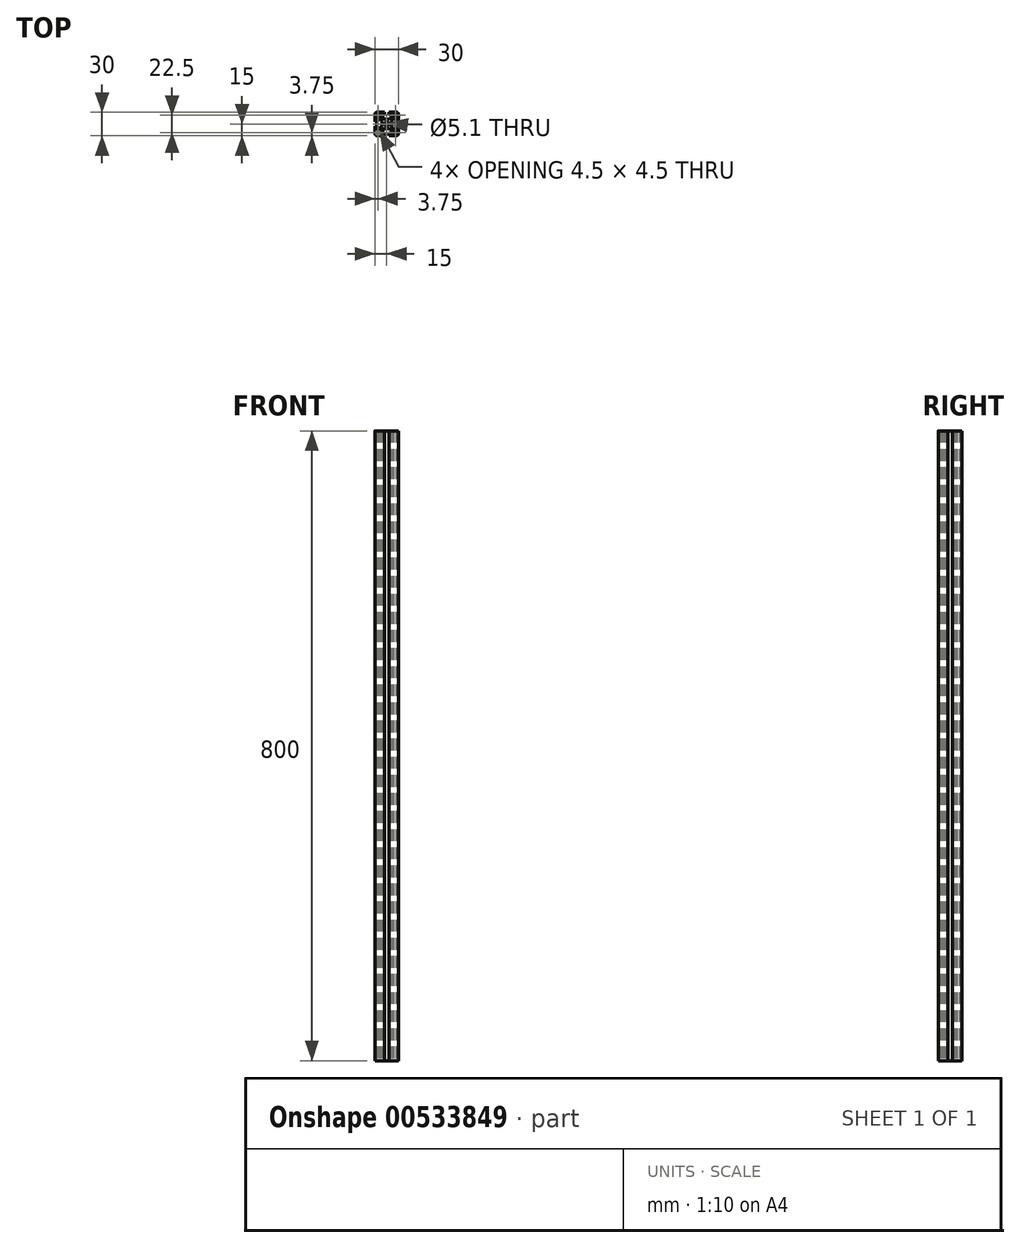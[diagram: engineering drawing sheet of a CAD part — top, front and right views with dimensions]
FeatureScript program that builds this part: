
annotation { "Feature Type Name" : "Feature", "Feature Type Description" : "" }
export const myFeature = defineFeature(function(context is Context, id is Id, definition is map)
    precondition{}
    {
        {
            var Q0;
            Q0=qCreatedBy(makeId("Top.planeOp"),FACE);
            var sketch = newSketch(context, id + "F0", { "sketchPlane" : qUnion([Q0])});
            skLineSegment(sketch, "E0", {"start": v(20, 4) * mm, "end": v(15.5, 4) * mm});
            skLineSegment(sketch, "E1", {"start": v(20, 16) * mm, "end": v(20, 4) * mm});
            skArc(sketch, "E2", {"start": v(16, 20) * mm, "mid": v(18.83, 18.83) * mm, "end": v(20, 16) * mm});
            skLineSegment(sketch, "E3", {"start": v(4, 20) * mm, "end": v(16, 20) * mm});
            skLineSegment(sketch, "E4", {"start": v(4, 20) * mm, "end": v(4, 15.5) * mm});
            skLineSegment(sketch, "E5", {"start": v(4, 15.5) * mm, "end": v(6.72, 15.5) * mm});
            skLineSegment(sketch, "E6", {"start": v(6.72, 17.35) * mm, "end": v(6.72, 15.5) * mm});
            skLineSegment(sketch, "E7", {"start": v(10.22, 17.35) * mm, "end": v(6.72, 17.35) * mm});
            skLineSegment(sketch, "E8", {"start": v(10.22, 12) * mm, "end": v(10.22, 17.35) * mm});
            skLineSegment(sketch, "E9", {"start": v(4, 7.75) * mm, "end": v(10.22, 12) * mm});
            skLineSegment(sketch, "E10", {"start": v(-4, 7.75) * mm, "end": v(4, 7.75) * mm});
            skLineSegment(sketch, "E11", {"start": v(-4, 7.75) * mm, "end": v(-10.22, 12) * mm});
            skLineSegment(sketch, "E12", {"start": v(-10.22, 12) * mm, "end": v(-10.22, 17.35) * mm});
            skLineSegment(sketch, "E13", {"start": v(-10.22, 17.35) * mm, "end": v(-6.72, 17.35) * mm});
            skLineSegment(sketch, "E14", {"start": v(-6.72, 15.5) * mm, "end": v(-6.72, 17.35) * mm});
            skLineSegment(sketch, "E15", {"start": v(-4, 15.5) * mm, "end": v(-6.72, 15.5) * mm});
            skLineSegment(sketch, "E16", {"start": v(-4, 20) * mm, "end": v(-4, 15.5) * mm});
            skLineSegment(sketch, "E17", {"start": v(-16, 20) * mm, "end": v(-4, 20) * mm});
            skArc(sketch, "E18", {"start": v(-16, 20) * mm, "mid": v(-18.83, 18.83) * mm, "end": v(-20, 16) * mm});
            skLineSegment(sketch, "E19", {"start": v(-20, 16) * mm, "end": v(-20, 4) * mm});
            skLineSegment(sketch, "E20", {"start": v(-20, 4) * mm, "end": v(-15.5, 4) * mm});
            skLineSegment(sketch, "E21", {"start": v(-15.5, 4) * mm, "end": v(-15.5, 6.72) * mm});
            skLineSegment(sketch, "E22", {"start": v(-17.35, 6.72) * mm, "end": v(-15.5, 6.72) * mm});
            skLineSegment(sketch, "E23", {"start": v(-17.35, 10.22) * mm, "end": v(-17.35, 6.72) * mm});
            skLineSegment(sketch, "E24", {"start": v(-12, 10.22) * mm, "end": v(-17.35, 10.22) * mm});
            skLineSegment(sketch, "E25", {"start": v(-7.75, 4) * mm, "end": v(-12, 10.22) * mm});
            skLineSegment(sketch, "E26", {"start": v(-7.75, -4) * mm, "end": v(-7.75, 4) * mm});
            skLineSegment(sketch, "E27", {"start": v(-7.75, -4) * mm, "end": v(-12, -10.22) * mm});
            skLineSegment(sketch, "E28", {"start": v(-12, -10.22) * mm, "end": v(-17.35, -10.22) * mm});
            skLineSegment(sketch, "E29", {"start": v(-17.35, -10.22) * mm, "end": v(-17.35, -6.72) * mm});
            skLineSegment(sketch, "E30", {"start": v(-17.35, -6.72) * mm, "end": v(-15.5, -6.72) * mm});
            skLineSegment(sketch, "E31", {"start": v(-15.5, -4) * mm, "end": v(-15.5, -6.72) * mm});
            skLineSegment(sketch, "E32", {"start": v(-20, -4) * mm, "end": v(-15.5, -4) * mm});
            skLineSegment(sketch, "E33", {"start": v(-20, -4) * mm, "end": v(-20, -16) * mm});
            skArc(sketch, "E34", {"start": v(-20, -16) * mm, "mid": v(-18.83, -18.83) * mm, "end": v(-16, -20) * mm});
            skLineSegment(sketch, "E35", {"start": v(-16, -20) * mm, "end": v(-4, -20) * mm});
            skLineSegment(sketch, "E36", {"start": v(-4, -20) * mm, "end": v(-4, -15.5) * mm});
            skLineSegment(sketch, "E37", {"start": v(-4, -15.5) * mm, "end": v(-6.72, -15.5) * mm});
            skLineSegment(sketch, "E38", {"start": v(-6.72, -17.35) * mm, "end": v(-6.72, -15.5) * mm});
            skLineSegment(sketch, "E39", {"start": v(-10.22, -17.35) * mm, "end": v(-6.72, -17.35) * mm});
            skLineSegment(sketch, "E40", {"start": v(-10.22, -12) * mm, "end": v(-10.22, -17.35) * mm});
            skLineSegment(sketch, "E41", {"start": v(-4, -7.75) * mm, "end": v(-10.22, -12) * mm});
            skLineSegment(sketch, "E42", {"start": v(4, -7.75) * mm, "end": v(-4, -7.75) * mm});
            skLineSegment(sketch, "E43", {"start": v(4, -7.75) * mm, "end": v(10.22, -12) * mm});
            skLineSegment(sketch, "E44", {"start": v(10.22, -12) * mm, "end": v(10.22, -17.35) * mm});
            skLineSegment(sketch, "E45", {"start": v(10.22, -17.35) * mm, "end": v(6.72, -17.35) * mm});
            skLineSegment(sketch, "E46", {"start": v(6.72, -15.5) * mm, "end": v(6.72, -17.35) * mm});
            skLineSegment(sketch, "E47", {"start": v(4, -15.5) * mm, "end": v(6.72, -15.5) * mm});
            skLineSegment(sketch, "E48", {"start": v(4, -20) * mm, "end": v(4, -15.5) * mm});
            skLineSegment(sketch, "E49", {"start": v(4, -20) * mm, "end": v(16, -20) * mm});
            skArc(sketch, "E50", {"start": v(16, -20) * mm, "mid": v(18.83, -18.83) * mm, "end": v(20, -16) * mm});
            skLineSegment(sketch, "E51", {"start": v(20, -4) * mm, "end": v(20, -16) * mm});
            skLineSegment(sketch, "E52", {"start": v(20, -4) * mm, "end": v(15.5, -4) * mm});
            skLineSegment(sketch, "E53", {"start": v(15.5, -4) * mm, "end": v(15.5, -6.72) * mm});
            skLineSegment(sketch, "E54", {"start": v(17.35, -6.72) * mm, "end": v(15.5, -6.72) * mm});
            skLineSegment(sketch, "E55", {"start": v(17.35, -10.22) * mm, "end": v(17.35, -6.72) * mm});
            skLineSegment(sketch, "E56", {"start": v(12, -10.22) * mm, "end": v(17.35, -10.22) * mm});
            skLineSegment(sketch, "E57", {"start": v(7.75, -4) * mm, "end": v(12, -10.22) * mm});
            skLineSegment(sketch, "E58", {"start": v(7.75, 4) * mm, "end": v(7.75, -4) * mm});
            skLineSegment(sketch, "E59", {"start": v(7.75, 4) * mm, "end": v(12, 10.22) * mm});
            skLineSegment(sketch, "E60", {"start": v(12, 10.22) * mm, "end": v(17.35, 10.22) * mm});
            skLineSegment(sketch, "E61", {"start": v(17.35, 10.22) * mm, "end": v(17.35, 6.72) * mm});
            skLineSegment(sketch, "E62", {"start": v(15.5, 6.72) * mm, "end": v(17.35, 6.72) * mm});
            skLineSegment(sketch, "E63", {"start": v(15.5, 4) * mm, "end": v(15.5, 6.72) * mm});
            skLineSegment(sketch, "E64", {"start": v(18, 12) * mm, "end": v(18, 16) * mm});
            skLineSegment(sketch, "E65", {"start": v(12, 12) * mm, "end": v(18, 12) * mm});
            skLineSegment(sketch, "E66", {"start": v(12, 18) * mm, "end": v(12, 12) * mm});
            skLineSegment(sketch, "E67", {"start": v(16, 18) * mm, "end": v(12, 18) * mm});
            skArc(sketch, "E68", {"start": v(18, 16) * mm, "mid": v(17.41, 17.41) * mm, "end": v(16, 18) * mm});
            skLineSegment(sketch, "E69", {"start": v(-18, -12) * mm, "end": v(-18, -16) * mm});
            skLineSegment(sketch, "E70", {"start": v(-12, -12) * mm, "end": v(-18, -12) * mm});
            skLineSegment(sketch, "E71", {"start": v(-12, -18) * mm, "end": v(-12, -12) * mm});
            skLineSegment(sketch, "E72", {"start": v(-16, -18) * mm, "end": v(-12, -18) * mm});
            skArc(sketch, "E73", {"start": v(-18, -16) * mm, "mid": v(-17.41, -17.41) * mm, "end": v(-16, -18) * mm});
            skLineSegment(sketch, "E74", {"start": v(12, -18) * mm, "end": v(16, -18) * mm});
            skLineSegment(sketch, "E75", {"start": v(12, -12) * mm, "end": v(12, -18) * mm});
            skLineSegment(sketch, "E76", {"start": v(18, -12) * mm, "end": v(12, -12) * mm});
            skLineSegment(sketch, "E77", {"start": v(18, -16) * mm, "end": v(18, -12) * mm});
            skArc(sketch, "E78", {"start": v(16, -18) * mm, "mid": v(17.41, -17.41) * mm, "end": v(18, -16) * mm});
            skLineSegment(sketch, "E79", {"start": v(-12, 18) * mm, "end": v(-16, 18) * mm});
            skLineSegment(sketch, "E80", {"start": v(-12, 12) * mm, "end": v(-12, 18) * mm});
            skLineSegment(sketch, "E81", {"start": v(-18, 12) * mm, "end": v(-12, 12) * mm});
            skLineSegment(sketch, "E82", {"start": v(-18, 16) * mm, "end": v(-18, 12) * mm});
            skArc(sketch, "E83", {"start": v(-16, 18) * mm, "mid": v(-17.41, 17.41) * mm, "end": v(-18, 16) * mm});
            skCircle(sketch, "E84", {"center": v(0, 0) * mm, "radius": 3.4 * mm});
            skSolve(sketch);
        }
        {
            var Q0;
            Q0=makeQuery(id+"F0.imprint","IMPRINT",FACE,{"disambiguationData":[TD([[makeQuery(id+"F0.imprint","IMPRINT",EDGE,{"derivedFrom":sQuery(id+"F0.wireOp",EDGE,"E0")}),-1.0]])]});
            extrude(context, id + "F1", {"entities" : qUnion([Q0]), "depth" : 400 * mm, "offsetDistance" : 25 * mm});
        }
        {
            var Q0;
            Q0=makeQuery(id+"F1.opExtrude","SWEPT_BODY",BODY,{"disambiguationData":[OSD([sQuery(id+"F0.wireOp",EDGE,"E0"),sQuery(id+"F0.wireOp",EDGE,"E1"),sQuery(id+"F0.wireOp",EDGE,"E2"),sQuery(id+"F0.wireOp",EDGE,"E3"),sQuery(id+"F0.wireOp",EDGE,"E4"),sQuery(id+"F0.wireOp",EDGE,"E5"),sQuery(id+"F0.wireOp",EDGE,"E6"),sQuery(id+"F0.wireOp",EDGE,"E7"),sQuery(id+"F0.wireOp",EDGE,"E8"),sQuery(id+"F0.wireOp",EDGE,"E9"),sQuery(id+"F0.wireOp",EDGE,"E10"),sQuery(id+"F0.wireOp",EDGE,"E11"),sQuery(id+"F0.wireOp",EDGE,"E12"),sQuery(id+"F0.wireOp",EDGE,"E13"),sQuery(id+"F0.wireOp",EDGE,"E14"),sQuery(id+"F0.wireOp",EDGE,"E15"),sQuery(id+"F0.wireOp",EDGE,"E16"),sQuery(id+"F0.wireOp",EDGE,"E17"),sQuery(id+"F0.wireOp",EDGE,"E18"),sQuery(id+"F0.wireOp",EDGE,"E19"),sQuery(id+"F0.wireOp",EDGE,"E20"),sQuery(id+"F0.wireOp",EDGE,"E21"),sQuery(id+"F0.wireOp",EDGE,"E22"),sQuery(id+"F0.wireOp",EDGE,"E23"),sQuery(id+"F0.wireOp",EDGE,"E24"),sQuery(id+"F0.wireOp",EDGE,"E25"),sQuery(id+"F0.wireOp",EDGE,"E26"),sQuery(id+"F0.wireOp",EDGE,"E27"),sQuery(id+"F0.wireOp",EDGE,"E28"),sQuery(id+"F0.wireOp",EDGE,"E29"),sQuery(id+"F0.wireOp",EDGE,"E30"),sQuery(id+"F0.wireOp",EDGE,"E31"),sQuery(id+"F0.wireOp",EDGE,"E32"),sQuery(id+"F0.wireOp",EDGE,"E33"),sQuery(id+"F0.wireOp",EDGE,"E34"),sQuery(id+"F0.wireOp",EDGE,"E35"),sQuery(id+"F0.wireOp",EDGE,"E36"),sQuery(id+"F0.wireOp",EDGE,"E37"),sQuery(id+"F0.wireOp",EDGE,"E38"),sQuery(id+"F0.wireOp",EDGE,"E39"),sQuery(id+"F0.wireOp",EDGE,"E40"),sQuery(id+"F0.wireOp",EDGE,"E41"),sQuery(id+"F0.wireOp",EDGE,"E42"),sQuery(id+"F0.wireOp",EDGE,"E43"),sQuery(id+"F0.wireOp",EDGE,"E44"),sQuery(id+"F0.wireOp",EDGE,"E45"),sQuery(id+"F0.wireOp",EDGE,"E46"),sQuery(id+"F0.wireOp",EDGE,"E47"),sQuery(id+"F0.wireOp",EDGE,"E48"),sQuery(id+"F0.wireOp",EDGE,"E49"),sQuery(id+"F0.wireOp",EDGE,"E50"),sQuery(id+"F0.wireOp",EDGE,"E51"),sQuery(id+"F0.wireOp",EDGE,"E52"),sQuery(id+"F0.wireOp",EDGE,"E53"),sQuery(id+"F0.wireOp",EDGE,"E54"),sQuery(id+"F0.wireOp",EDGE,"E55"),sQuery(id+"F0.wireOp",EDGE,"E56"),sQuery(id+"F0.wireOp",EDGE,"E57"),sQuery(id+"F0.wireOp",EDGE,"E58"),sQuery(id+"F0.wireOp",EDGE,"E59"),sQuery(id+"F0.wireOp",EDGE,"E60"),sQuery(id+"F0.wireOp",EDGE,"E61"),sQuery(id+"F0.wireOp",EDGE,"E62"),sQuery(id+"F0.wireOp",EDGE,"E63"),sQuery(id+"F0.wireOp",EDGE,"E64"),sQuery(id+"F0.wireOp",EDGE,"E65"),sQuery(id+"F0.wireOp",EDGE,"E66"),sQuery(id+"F0.wireOp",EDGE,"E67"),sQuery(id+"F0.wireOp",EDGE,"E68"),sQuery(id+"F0.wireOp",EDGE,"E69"),sQuery(id+"F0.wireOp",EDGE,"E70"),sQuery(id+"F0.wireOp",EDGE,"E71"),sQuery(id+"F0.wireOp",EDGE,"E72"),sQuery(id+"F0.wireOp",EDGE,"E73"),sQuery(id+"F0.wireOp",EDGE,"E74"),sQuery(id+"F0.wireOp",EDGE,"E75"),sQuery(id+"F0.wireOp",EDGE,"E76"),sQuery(id+"F0.wireOp",EDGE,"E77"),sQuery(id+"F0.wireOp",EDGE,"E78"),sQuery(id+"F0.wireOp",EDGE,"E79"),sQuery(id+"F0.wireOp",EDGE,"E80"),sQuery(id+"F0.wireOp",EDGE,"E81"),sQuery(id+"F0.wireOp",EDGE,"E82"),sQuery(id+"F0.wireOp",EDGE,"E83"),sQuery(id+"F0.wireOp",EDGE,"E84")])]});
            var Q1;
            Q1=makeQuery(id+"F1.opExtrude","CAP_VERTEX",VERTEX,{"disambiguationData":[OSD([sQuery(id+"F0.wireOp",EDGE,"E51"),sQuery(id+"F0.wireOp",EDGE,"E52")])],"isStart":true});
            transform(context, id + "F2", {"entities" : qUnion([Q0]), "transformType" : TransformType.SCALE_UNIFORMLY, "scale" : 3 / 4, "scalePoint" : qUnion([Q1]), "makeCopy" : false});
        }
        {
            var Q0;
            Q0=makeQuery(id+"F1.opExtrude","CAP_FACE",FACE,{"disambiguationData":[OSD([sQuery(id+"F0.wireOp",EDGE,"E0"),sQuery(id+"F0.wireOp",EDGE,"E1"),sQuery(id+"F0.wireOp",EDGE,"E2"),sQuery(id+"F0.wireOp",EDGE,"E3"),sQuery(id+"F0.wireOp",EDGE,"E4"),sQuery(id+"F0.wireOp",EDGE,"E5"),sQuery(id+"F0.wireOp",EDGE,"E6"),sQuery(id+"F0.wireOp",EDGE,"E7"),sQuery(id+"F0.wireOp",EDGE,"E8"),sQuery(id+"F0.wireOp",EDGE,"E9"),sQuery(id+"F0.wireOp",EDGE,"E10"),sQuery(id+"F0.wireOp",EDGE,"E11"),sQuery(id+"F0.wireOp",EDGE,"E12"),sQuery(id+"F0.wireOp",EDGE,"E13"),sQuery(id+"F0.wireOp",EDGE,"E14"),sQuery(id+"F0.wireOp",EDGE,"E15"),sQuery(id+"F0.wireOp",EDGE,"E16"),sQuery(id+"F0.wireOp",EDGE,"E17"),sQuery(id+"F0.wireOp",EDGE,"E18"),sQuery(id+"F0.wireOp",EDGE,"E19"),sQuery(id+"F0.wireOp",EDGE,"E20"),sQuery(id+"F0.wireOp",EDGE,"E21"),sQuery(id+"F0.wireOp",EDGE,"E22"),sQuery(id+"F0.wireOp",EDGE,"E23"),sQuery(id+"F0.wireOp",EDGE,"E24"),sQuery(id+"F0.wireOp",EDGE,"E25"),sQuery(id+"F0.wireOp",EDGE,"E26"),sQuery(id+"F0.wireOp",EDGE,"E27"),sQuery(id+"F0.wireOp",EDGE,"E28"),sQuery(id+"F0.wireOp",EDGE,"E29"),sQuery(id+"F0.wireOp",EDGE,"E30"),sQuery(id+"F0.wireOp",EDGE,"E31"),sQuery(id+"F0.wireOp",EDGE,"E32"),sQuery(id+"F0.wireOp",EDGE,"E33"),sQuery(id+"F0.wireOp",EDGE,"E34"),sQuery(id+"F0.wireOp",EDGE,"E35"),sQuery(id+"F0.wireOp",EDGE,"E36"),sQuery(id+"F0.wireOp",EDGE,"E37"),sQuery(id+"F0.wireOp",EDGE,"E38"),sQuery(id+"F0.wireOp",EDGE,"E39"),sQuery(id+"F0.wireOp",EDGE,"E40"),sQuery(id+"F0.wireOp",EDGE,"E41"),sQuery(id+"F0.wireOp",EDGE,"E42"),sQuery(id+"F0.wireOp",EDGE,"E43"),sQuery(id+"F0.wireOp",EDGE,"E44"),sQuery(id+"F0.wireOp",EDGE,"E45"),sQuery(id+"F0.wireOp",EDGE,"E46"),sQuery(id+"F0.wireOp",EDGE,"E47"),sQuery(id+"F0.wireOp",EDGE,"E48"),sQuery(id+"F0.wireOp",EDGE,"E49"),sQuery(id+"F0.wireOp",EDGE,"E50"),sQuery(id+"F0.wireOp",EDGE,"E51"),sQuery(id+"F0.wireOp",EDGE,"E52"),sQuery(id+"F0.wireOp",EDGE,"E53"),sQuery(id+"F0.wireOp",EDGE,"E54"),sQuery(id+"F0.wireOp",EDGE,"E55"),sQuery(id+"F0.wireOp",EDGE,"E56"),sQuery(id+"F0.wireOp",EDGE,"E57"),sQuery(id+"F0.wireOp",EDGE,"E58"),sQuery(id+"F0.wireOp",EDGE,"E59"),sQuery(id+"F0.wireOp",EDGE,"E60"),sQuery(id+"F0.wireOp",EDGE,"E61"),sQuery(id+"F0.wireOp",EDGE,"E62"),sQuery(id+"F0.wireOp",EDGE,"E63"),sQuery(id+"F0.wireOp",EDGE,"E64"),sQuery(id+"F0.wireOp",EDGE,"E65"),sQuery(id+"F0.wireOp",EDGE,"E66"),sQuery(id+"F0.wireOp",EDGE,"E67"),sQuery(id+"F0.wireOp",EDGE,"E68"),sQuery(id+"F0.wireOp",EDGE,"E69"),sQuery(id+"F0.wireOp",EDGE,"E70"),sQuery(id+"F0.wireOp",EDGE,"E71"),sQuery(id+"F0.wireOp",EDGE,"E72"),sQuery(id+"F0.wireOp",EDGE,"E73"),sQuery(id+"F0.wireOp",EDGE,"E74"),sQuery(id+"F0.wireOp",EDGE,"E75"),sQuery(id+"F0.wireOp",EDGE,"E76"),sQuery(id+"F0.wireOp",EDGE,"E77"),sQuery(id+"F0.wireOp",EDGE,"E78"),sQuery(id+"F0.wireOp",EDGE,"E79"),sQuery(id+"F0.wireOp",EDGE,"E80"),sQuery(id+"F0.wireOp",EDGE,"E81"),sQuery(id+"F0.wireOp",EDGE,"E82"),sQuery(id+"F0.wireOp",EDGE,"E83"),sQuery(id+"F0.wireOp",EDGE,"E84")])],"isStart":false});
            extrude(context, id + "F3", {"entities" : qUnion([Q0]), "operationType" : NewBodyOperationType.ADD, "depth" : 100 * mm, "offsetDistance" : 25 * mm});
        }
        {
            var Q0;
            Q0=makeQuery(id+"F3.opExtrude","CAP_FACE",FACE,{"disambiguationData":[OSD([sQuery(id+"F0.wireOp",EDGE,"E0"),sQuery(id+"F0.wireOp",EDGE,"E1"),sQuery(id+"F0.wireOp",EDGE,"E2"),sQuery(id+"F0.wireOp",EDGE,"E3"),sQuery(id+"F0.wireOp",EDGE,"E4"),sQuery(id+"F0.wireOp",EDGE,"E5"),sQuery(id+"F0.wireOp",EDGE,"E6"),sQuery(id+"F0.wireOp",EDGE,"E7"),sQuery(id+"F0.wireOp",EDGE,"E8"),sQuery(id+"F0.wireOp",EDGE,"E9"),sQuery(id+"F0.wireOp",EDGE,"E10"),sQuery(id+"F0.wireOp",EDGE,"E11"),sQuery(id+"F0.wireOp",EDGE,"E12"),sQuery(id+"F0.wireOp",EDGE,"E13"),sQuery(id+"F0.wireOp",EDGE,"E14"),sQuery(id+"F0.wireOp",EDGE,"E15"),sQuery(id+"F0.wireOp",EDGE,"E16"),sQuery(id+"F0.wireOp",EDGE,"E17"),sQuery(id+"F0.wireOp",EDGE,"E18"),sQuery(id+"F0.wireOp",EDGE,"E19"),sQuery(id+"F0.wireOp",EDGE,"E20"),sQuery(id+"F0.wireOp",EDGE,"E21"),sQuery(id+"F0.wireOp",EDGE,"E22"),sQuery(id+"F0.wireOp",EDGE,"E23"),sQuery(id+"F0.wireOp",EDGE,"E24"),sQuery(id+"F0.wireOp",EDGE,"E25"),sQuery(id+"F0.wireOp",EDGE,"E26"),sQuery(id+"F0.wireOp",EDGE,"E27"),sQuery(id+"F0.wireOp",EDGE,"E28"),sQuery(id+"F0.wireOp",EDGE,"E29"),sQuery(id+"F0.wireOp",EDGE,"E30"),sQuery(id+"F0.wireOp",EDGE,"E31"),sQuery(id+"F0.wireOp",EDGE,"E32"),sQuery(id+"F0.wireOp",EDGE,"E33"),sQuery(id+"F0.wireOp",EDGE,"E34"),sQuery(id+"F0.wireOp",EDGE,"E35"),sQuery(id+"F0.wireOp",EDGE,"E36"),sQuery(id+"F0.wireOp",EDGE,"E37"),sQuery(id+"F0.wireOp",EDGE,"E38"),sQuery(id+"F0.wireOp",EDGE,"E39"),sQuery(id+"F0.wireOp",EDGE,"E40"),sQuery(id+"F0.wireOp",EDGE,"E41"),sQuery(id+"F0.wireOp",EDGE,"E42"),sQuery(id+"F0.wireOp",EDGE,"E43"),sQuery(id+"F0.wireOp",EDGE,"E44"),sQuery(id+"F0.wireOp",EDGE,"E45"),sQuery(id+"F0.wireOp",EDGE,"E46"),sQuery(id+"F0.wireOp",EDGE,"E47"),sQuery(id+"F0.wireOp",EDGE,"E48"),sQuery(id+"F0.wireOp",EDGE,"E49"),sQuery(id+"F0.wireOp",EDGE,"E50"),sQuery(id+"F0.wireOp",EDGE,"E51"),sQuery(id+"F0.wireOp",EDGE,"E52"),sQuery(id+"F0.wireOp",EDGE,"E53"),sQuery(id+"F0.wireOp",EDGE,"E54"),sQuery(id+"F0.wireOp",EDGE,"E55"),sQuery(id+"F0.wireOp",EDGE,"E56"),sQuery(id+"F0.wireOp",EDGE,"E57"),sQuery(id+"F0.wireOp",EDGE,"E58"),sQuery(id+"F0.wireOp",EDGE,"E59"),sQuery(id+"F0.wireOp",EDGE,"E60"),sQuery(id+"F0.wireOp",EDGE,"E61"),sQuery(id+"F0.wireOp",EDGE,"E62"),sQuery(id+"F0.wireOp",EDGE,"E63"),sQuery(id+"F0.wireOp",EDGE,"E64"),sQuery(id+"F0.wireOp",EDGE,"E65"),sQuery(id+"F0.wireOp",EDGE,"E66"),sQuery(id+"F0.wireOp",EDGE,"E67"),sQuery(id+"F0.wireOp",EDGE,"E68"),sQuery(id+"F0.wireOp",EDGE,"E69"),sQuery(id+"F0.wireOp",EDGE,"E70"),sQuery(id+"F0.wireOp",EDGE,"E71"),sQuery(id+"F0.wireOp",EDGE,"E72"),sQuery(id+"F0.wireOp",EDGE,"E73"),sQuery(id+"F0.wireOp",EDGE,"E74"),sQuery(id+"F0.wireOp",EDGE,"E75"),sQuery(id+"F0.wireOp",EDGE,"E76"),sQuery(id+"F0.wireOp",EDGE,"E77"),sQuery(id+"F0.wireOp",EDGE,"E78"),sQuery(id+"F0.wireOp",EDGE,"E79"),sQuery(id+"F0.wireOp",EDGE,"E80"),sQuery(id+"F0.wireOp",EDGE,"E81"),sQuery(id+"F0.wireOp",EDGE,"E82"),sQuery(id+"F0.wireOp",EDGE,"E83"),sQuery(id+"F0.wireOp",EDGE,"E84")])],"isStart":false});
            extrude(context, id + "F4", {"entities" : qUnion([Q0]), "operationType" : NewBodyOperationType.ADD, "depth" : 400 * mm, "offsetDistance" : 25 * mm});
        }
    });
